# Revit family: Hager-FW-Surface_mounted-IP30-With_Cover-With_DIN-Hosted-GB-en
name_source: partatom
category: Electrical Equipment
units: mm (PartAtom-declared; Revit-internal decimal feet)

## family parameters
Cut with Voids When Loaded = No
Host = Face
Maintain Annotation Orientation = Yes
Panel Configuration = Two Columns, Circuits Across
Part Type = Panelboard
Room Calculation Point = No
Round Connector Dimension = Use Diameter
Shared = No

## types (9) — shared parameters
BC_MODEL_ID = 1554237
BC_OBJECT_ID = 513836
BC_OBJECT_VERSION = #1
Code hager = ADD-EC000214_EU
EF000003 - Mounting method = Surface mounted
EF000007 - Colour = White
EF000024 - UV resistant = No
EF000049 - Depth = 150 mm
EF000116 - RAL number = 9010
EF000118 - With mounting plate = No
EF001062 - EMC-version = No
EF001088 - Extension possible = Yes
EF001134 - With DIN-rail = Yes
EF004462 - Type of closure = Other
EF005474 - Degree of protection (IP rating) = IP30
EF006244 - Transparent cover/door = No
EF006306 - With lock = No
EF009212 - Cover model = Closed
EF015776 - Earthing terminal block = Yes
EF015777 - Neutral terminal block = No
EF015941 - Signal passing door = No
ETIM class code = EC000214
ETIM class name = Small distribution board
HG000001-Number of columns = 1
HG000002-With door or cover = Yes
HG000003-Range = FW
HG000005-Thickness = 2 mm  [stored 0.00656168 ft]
HG000006-Flush mounted = No
HG000009-Double swing door = No
HG000010-Asymmetric doors = No
HG000011-Empty rows from bottom = No
HG000012-Door swing angle = 90.00°
HG000013-Door on the left = No
HG000014-Door on the right = Yes
HG000015-Clearance visibility = Yes
HG000016-Door 3D visibility = Yes
HG000017-Distance between poles = 18 mm  [stored 0.0590551 ft]
HG000060-RAL-number = 9010
HG000099-Onfly Template ID = 507532
Manufacturer = Hager
Name = FW-Surface_mounted-IP30-With_Cover-With_DIN-GB
Name BIM&CO = Electricity
Name hager = ADD_Enclosures_EC000214
Uniformat = Low Tension Service & Dist.
Uniformat code = D501001
zero-valued in all types: Default Elevation, EF000218 - Recess depth, EF000332 - Recess height, EF000846 - Recess width, EF001131 - Internal depth, HG000007-Number of empty columns, HG000008-Number of empty rows

## per-type parameters (varying)
| type | BC_VARIANT_ID | EF000008 - Width | EF000040 - Height | EF000266 - Number of rows | EF002950 - Width in number of modular spacings | HG000004-Manufacturer reference | HGEF000266-Number of rows | HGEF002950-Width in number of modular spacings |
| FW-Surface_mounted_W571_H641_D150_24_Modular_Spacing-FW324WT | 1178730 | 571 mm  [stored 1.87336 ft] | 641 mm  [stored 2.10302 ft] | 3 | 24 | FW324WT | 3 | 24 |
| FW-Surface_mounted_W571_H791_D150_24_Modular_Spacing-FW424WT | 1178731 | 571 mm  [stored 1.87336 ft] | 791 mm | 4 | 24 | FW424WT | 4 | 24 |
| FW-Surface_mounted_W787_H791_D150_36_Modular_Spacing-FW436WT | 1178732 | 787 mm  [stored 2.58202 ft] | 791 mm | 4 | 36 | FW436WT | 4 | 36 |
| FW-Surface_mounted_W355_H941_D150_12_Modular_Spacing-FW512WT | 1178736 | 355 mm | 941 mm | 5 | 12 | FW512WT | 5 | 12 |
| FW-Surface_mounted_W571_H941_D150_24_Modular_Spacing-FW524WT | 1178737 | 571 mm  [stored 1.87336 ft] | 941 mm | 5 | 24 | FW524WT | 5 | 24 |
| FW-Surface_mounted_W355_H1091_D150_12_Modular_Spacing-FW612WT | 1178738 | 355 mm | 1091 mm | 6 | 12 | FW612WT | 6 | 12 |
| FW-Surface_mounted_W571_H1091_D150_24_Modular_Spacing-FW624WT | 1178739 | 571 mm  [stored 1.87336 ft] | 1091 mm | 6 | 24 | FW624WT | 6 | 24 |
| FW-Surface_mounted_W787_H1091_D150_36_Modular_Spacing-FW636WT | 1178740 | 787 mm  [stored 2.58202 ft] | 1091 mm | 6 | 36 | FW636WT | 6 | 36 |
| FW-Surface_mounted_W787_H1241_D150_36_Modular_Spacing-FW736WT | 1178741 | 787 mm  [stored 2.58202 ft] | 1241 mm  [stored 4.07152 ft] | 7 | 36 | FW736WT | 7 | 36 |

note: column(s) folded — value = type name in every type: Reference

note: [stored X ft] marks values corroborated as IEEE doubles in the binary element streams (Revit-internal decimal feet)

## geometry (parser evidence)
native form markers: Sweep x15
no freeform markers — native parametric forms only
